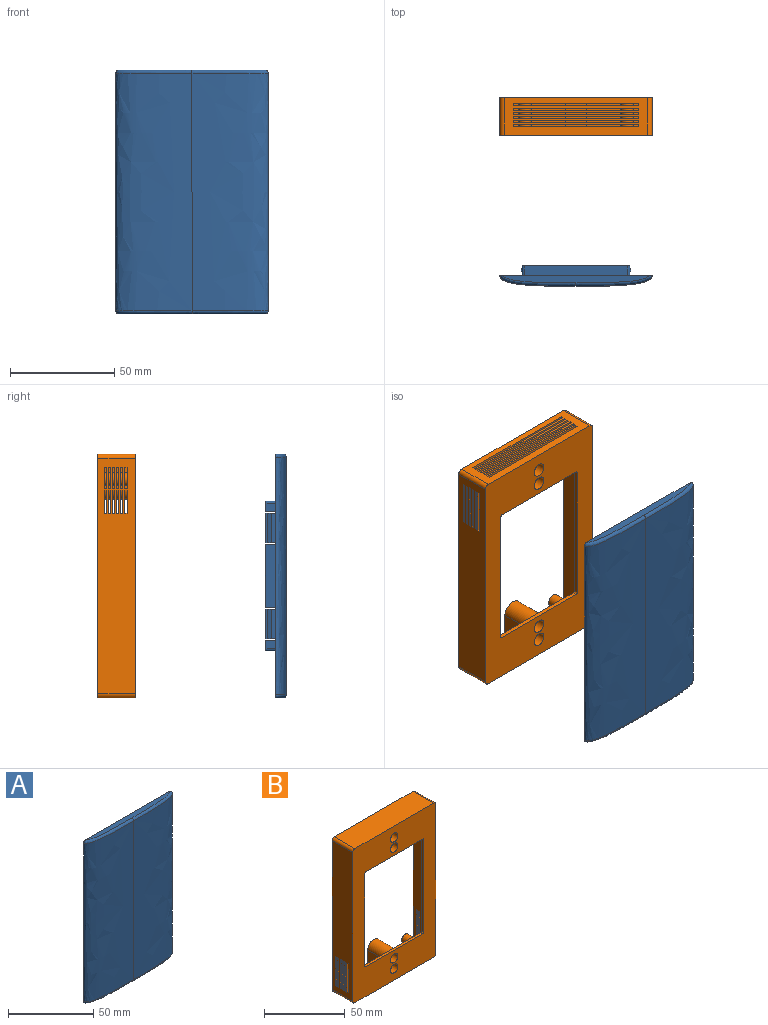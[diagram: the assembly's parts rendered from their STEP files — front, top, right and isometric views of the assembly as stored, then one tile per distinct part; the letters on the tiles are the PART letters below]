
ASSEMBLY  parts=2 mates=1
PART A: 93 faces, bbox 73.2x10.1x117.1 mm
  f0: plane 14x2.1mm, normal (1,0,0), area 29.4mm2, adj f37,f76,f78,f87
  f1: plane 14x0.7mm, normal (1,0,0), area 9.8mm2, adj f30,f74,f80,f86
  f2: plane 14x0.7mm, normal (-1,0,0), area 9.8mm2, adj f33,f67,f70,f84
  f3: plane 14x2.1mm, normal (-1,0,0), area 29.4mm2, adj f37,f65,f72,f81
  f4: plane 5x2.9mm, normal (1,0,0), area 14.5mm2, adj f37,f55,f56,f71
  f5: plane 30x5mm, normal (1,0,0), area 150mm2, adj f25,f37,f66,f69
  f6: plane 14x5mm, normal (1,0,0), area 70mm2, adj f22,f37,f67,f70
  f7: plane 14x5mm, normal (1,0,0), area 70mm2, adj f20,f37,f65,f72
  f8: plane 5x2.9mm, normal (-1,0,0), area 14.5mm2, adj f37,f45,f56,f79
  f9: plane 30x5mm, normal (-1,0,0), area 150mm2, adj f26,f37,f73,f77
  f10: plane 14x5mm, normal (-1,0,0), area 70mm2, adj f23,f37,f76,f78
  f11: plane 14x5mm, normal (-1,0,0), area 70mm2, adj f21,f37,f74,f80
  f12: plane 4.7x3.9mm, normal (-1,0,0), area 18.3mm2, adj f31,f37,f51,f71
  f13: plane 30x4.7mm, normal (-1,0,0), area 141mm2, adj f32,f37,f66,f69
  f14: plane 14x2.1mm, normal (-1,0,0), area 29.4mm2, adj f37,f67,f70,f83
  f15: plane 14x0.7mm, normal (-1,0,0), area 9.8mm2, adj f34,f65,f72,f82
  f16: plane 4.7x3.9mm, normal (1,0,0), area 18.3mm2, adj f27,f37,f53,f79
  f17: plane 30x4.7mm, normal (1,0,0), area 141mm2, adj f28,f37,f73,f77
  f18: plane 14x0.7mm, normal (1,0,0), area 9.8mm2, adj f29,f76,f78,f88
  f19: plane 14x2.1mm, normal (1,0,0), area 29.4mm2, adj f37,f74,f80,f85
  f20: plane 14x0.7mm, normal (0,1,0), area 9.8mm2, adj f7,f34,f65,f72
  f21: plane 14x0.7mm, normal (0,1,0), area 9.8mm2, adj f11,f30,f74,f80
  f22: plane 14x0.7mm, normal (0,1,0), area 9.8mm2, adj f6,f33,f67,f70
  f23: plane 14x0.7mm, normal (0,1,0), area 9.8mm2, adj f10,f29,f76,f78
  f24: plane 51.2x4.6mm, normal (0,1,0), area 41.5mm2, adj f40,f41,f42,f43,f44,f57,f58,f60
  f25: plane 30x0.7mm, normal (0,1,0), area 21mm2, adj f5,f32,f66,f69
  f26: plane 30x0.7mm, normal (0,1,0), area 21mm2, adj f9,f28,f73,f77
  f27: plane 3.9x0.3mm, normal (0.71,0.71,0), area 1.7mm2, adj f16,f56,f59,f79
  f28: plane 30x0.3mm, normal (0.71,0.71,0), area 12.7mm2, adj f17,f26,f73,f77
  f29: plane 14x0.3mm, normal (0.71,0.71,0), area 5.9mm2, adj f18,f23,f76,f78
  f30: plane 14x0.3mm, normal (0.71,0.71,0), area 5.9mm2, adj f1,f21,f74,f80
  f31: plane 3.9x0.3mm, normal (-0.71,0.71,0), area 1.7mm2, adj f12,f56,f63,f71
  f32: plane 30x0.3mm, normal (-0.71,0.71,0), area 12.7mm2, adj f13,f25,f66,f69
  f33: plane 14x0.3mm, normal (-0.71,0.71,0), area 5.9mm2, adj f2,f22,f67,f70
  f34: plane 14x0.3mm, normal (-0.71,0.71,0), area 5.9mm2, adj f15,f20,f65,f72
  f35: plane 70.1x3.55mm, normal (0,0,-1), area 209.6mm2, adj f37,f91,f92
  f36: plane 70.11x3.55mm, normal (0,0,1), area 209.6mm2, adj f37,f89,f90
  f37: plane 117.14x73.14mm, normal (0,1,0), area 8304mm2, adj f0,f3,f4,f5,f6,f7,f8,f9
  f38: bspline ~117x36.5mm, area 4331.7mm2, adj f37,f39,f89,f91
  f39: bspline ~117x36.5mm, area 4331.7mm2, adj f37,f38,f90,f92
  f40: plane 5x2.9mm, normal (1,0,0), area 14.5mm2, adj f24,f37,f41,f68
  f41: cylinder r=1mm len=5mm, axis (0,-1,0), area 7.9mm2, adj f24,f37,f40,f42
  f42: plane 47.8x5mm, normal (0,0,-1), area 239mm2, adj f24,f37,f41,f43
  f43: cylinder r=1mm len=5mm, axis (0,-1,0), area 7.9mm2, adj f24,f37,f42,f44
  f44: plane 5x2.9mm, normal (-1,0,0), area 14.5mm2, adj f24,f37,f43,f75
  f45: cylinder r=1mm len=5mm, axis (0,-1,0), area 7.9mm2, adj f8,f37,f46,f56
  f46: plane 47.8x5mm, normal (0,0,1), area 239mm2, adj f37,f45,f55,f56
  f47: cylinder r=1mm len=4.7mm, axis (0,-1,0), area 7.4mm2, adj f37,f48,f54,f58
  f48: plane 49.8x4.7mm, normal (0,0,1), area 234.1mm2, adj f37,f47,f49,f60
  f49: cylinder r=1mm len=4.7mm, axis (0,-1,0), area 7.4mm2, adj f37,f48,f50,f62
  f50: plane 4.7x3.9mm, normal (-1,0,0), area 18.3mm2, adj f37,f49,f64,f68
  f51: cylinder r=1mm len=4.7mm, axis (0,-1,0), area 7.4mm2, adj f12,f37,f52,f63
  f52: plane 49.8x4.7mm, normal (0,0,-1), area 234.1mm2, adj f37,f51,f53,f61
  f53: cylinder r=1mm len=4.7mm, axis (0,-1,0), area 7.4mm2, adj f16,f37,f52,f59
  f54: plane 4.7x3.9mm, normal (1,0,0), area 18.3mm2, adj f37,f47,f57,f75
  f55: cylinder r=1mm len=5mm, axis (0,-1,0), area 7.9mm2, adj f4,f37,f46,f56
  f56: plane 51.2x4.6mm, normal (0,1,0), area 41.5mm2, adj f4,f8,f27,f31,f45,f46,f55,f59
  f57: plane 3.9x0.3mm, normal (0.71,0.71,0), area 1.7mm2, adj f24,f54,f58,f75
  f58: cone r=1mm half-angle=45deg, axis (0,-1,0), area 0.6mm2, adj f24,f47,f57,f60
  f59: cone r=0.7mm half-angle=45deg, axis (0,-1,0), area 0.6mm2, adj f27,f53,f56,f61
  f60: plane 49.8x0.3mm, normal (0,0.71,0.71), area 21.1mm2, adj f24,f48,f58,f62
  f61: plane 49.8x0.3mm, normal (0,0.71,-0.71), area 21.1mm2, adj f52,f56,f59,f63
  f62: cone r=0.7mm half-angle=45deg, axis (0,-1,0), area 0.6mm2, adj f24,f49,f60,f64
  f63: cone r=1mm half-angle=45deg, axis (0,-1,0), area 0.6mm2, adj f31,f51,f56,f61
  f64: plane 3.9x0.3mm, normal (-0.71,0.71,0), area 1.7mm2, adj f24,f50,f62,f68
  f65: plane 5x1.48mm, normal (0,0,1), area 5.4mm2, adj f3,f7,f15,f20,f34,f37,f81,f82
  f66: plane 5x1mm, normal (0,0,-1), area 5mm2, adj f5,f13,f25,f32,f37
  f67: plane 5x1.48mm, normal (0,0,1), area 5.4mm2, adj f2,f6,f14,f22,f33,f37,f83,f84
  f68: plane 5x1mm, normal (0,0,-1), area 5mm2, adj f24,f37,f40,f50,f64
  f69: plane 5x1mm, normal (0,0,1), area 5mm2, adj f5,f13,f25,f32,f37
  f70: plane 5x1.48mm, normal (0,0,-1), area 5.4mm2, adj f2,f6,f14,f22,f33,f37,f83,f84
  f71: plane 5x1mm, normal (0,0,1), area 5mm2, adj f4,f12,f31,f37,f56
  f72: plane 5x1.48mm, normal (0,0,-1), area 5.4mm2, adj f3,f7,f15,f20,f34,f37,f81,f82
  f73: plane 5x1mm, normal (0,0,-1), area 5mm2, adj f9,f17,f26,f28,f37
  f74: plane 5x1.48mm, normal (0,0,1), area 5.4mm2, adj f1,f11,f19,f21,f30,f37,f85,f86
  f75: plane 5x1mm, normal (0,0,-1), area 5mm2, adj f24,f37,f44,f54,f57
  f76: plane 5x1.48mm, normal (0,0,1), area 5.4mm2, adj f0,f10,f18,f23,f29,f37,f87,f88
  f77: plane 5x1mm, normal (0,0,1), area 5mm2, adj f9,f17,f26,f28,f37
  f78: plane 5x1.48mm, normal (0,0,-1), area 5.4mm2, adj f0,f10,f18,f23,f29,f37,f87,f88
  f79: plane 5x1mm, normal (0,0,1), area 5mm2, adj f8,f16,f27,f37,f56
  f80: plane 5x1.48mm, normal (0,0,-1), area 5.4mm2, adj f1,f11,f19,f21,f30,f37,f85,f86
  f81: plane 14x0.48mm, normal (0,-1,0), area 6.6mm2, adj f3,f65,f72,f82
  f82: plane 14x1.9mm, normal (-0.97,0.24,0), area 27.4mm2, adj f15,f65,f72,f81
  f83: plane 14x0.48mm, normal (0,-1,0), area 6.6mm2, adj f14,f67,f70,f84
  f84: plane 14x1.9mm, normal (-0.97,0.24,0), area 27.4mm2, adj f2,f67,f70,f83
  f85: plane 14x0.48mm, normal (0,-1,0), area 6.6mm2, adj f19,f74,f80,f86
  f86: plane 14x1.9mm, normal (0.97,0.24,0), area 27.4mm2, adj f1,f74,f80,f85
  f87: plane 14x0.48mm, normal (0,-1,0), area 6.6mm2, adj f0,f76,f78,f88
  f88: plane 14x1.9mm, normal (0.97,0.24,0), area 27.4mm2, adj f18,f76,f78,f87
  f89: bspline ~50.22x5.07mm, area 84.3mm2, adj f36,f37,f38,f90
  f90: bspline ~39.95x5.07mm, area 84.3mm2, adj f36,f37,f39,f89
  f91: bspline ~50.22x5.07mm, area 84.3mm2, adj f35,f37,f38,f92
  f92: bspline ~39.95x5.07mm, area 84.3mm2, adj f35,f37,f39,f91
PART B: 141 faces, bbox 73x18x117 mm
  f0: plane 113x18mm, normal (-1,0,0), area 1902mm2, adj f8,f9,f91,f92,f93,f94,f95,f96
  f1: plane 109x16mm, normal (1,0,0), area 1612mm2, adj f8,f68,f86,f87,f93,f94,f95,f96
  f2: plane 10.5x1mm, normal (0,0,-1), area 10.5mm2, adj f13,f15,f64,f66
  f3: plane 10.5x1mm, normal (0,0,-1), area 10.5mm2, adj f17,f19,f64,f66
  f4: plane 10.5x1mm, normal (0,0,-1), area 10.5mm2, adj f21,f23,f64,f66
  f5: plane 10.5x1mm, normal (0,0,-1), area 10.5mm2, adj f25,f27,f64,f66
  f6: plane 10.5x1mm, normal (0,0,-1), area 10.5mm2, adj f29,f31,f64,f66
  f7: plane 10.5x1mm, normal (0,0,-1), area 10.5mm2, adj f34,f36,f64,f66
  f8: plane 117x73mm, normal (0,1,0), area 1084.8mm2, adj f0,f1,f10,f11,f12,f53,f54,f55
  f9: plane 117x73mm, normal (0,-1,0), area 4661.7mm2, adj f0,f10,f11,f12,f37,f38,f39,f40
  f10: plane 69x18mm, normal (0,0,-1), area 882mm2, adj f8,f9,f13,f14,f15,f16,f17,f18
  f11: plane 113x18mm, normal (1,0,0), area 1902mm2, adj f8,f9,f89,f90,f117,f118,f119,f120
  f12: plane 69x18mm, normal (0,0,1), area 1242mm2, adj f8,f9,f90,f91
  f13: plane 60x2mm, normal (0,1,0), area 120mm2, adj f2,f10,f14,f16,f63,f67
  f14: plane 2x1mm, normal (1,0,0), area 2mm2, adj f10,f13,f15,f63
  f15: plane 60x2mm, normal (0,-1,0), area 120mm2, adj f2,f10,f14,f16,f63,f67
  f16: plane 2x1mm, normal (-1,0,0), area 2mm2, adj f10,f13,f15,f67
  f17: plane 60x2mm, normal (0,1,0), area 120mm2, adj f3,f10,f18,f20,f63,f67
  f18: plane 2x1mm, normal (1,0,0), area 2mm2, adj f10,f17,f19,f63
  f19: plane 60x2mm, normal (0,-1,0), area 120mm2, adj f3,f10,f18,f20,f63,f67
  f20: plane 2x1mm, normal (-1,0,0), area 2mm2, adj f10,f17,f19,f67
  f21: plane 60x2mm, normal (0,1,0), area 120mm2, adj f4,f10,f22,f24,f63,f67
  f22: plane 2x1mm, normal (1,0,0), area 2mm2, adj f10,f21,f23,f63
  f23: plane 60x2mm, normal (0,-1,0), area 120mm2, adj f4,f10,f22,f24,f63,f67
  f24: plane 2x1mm, normal (-1,0,0), area 2mm2, adj f10,f21,f23,f67
  f25: plane 60x2mm, normal (0,1,0), area 120mm2, adj f5,f10,f26,f28,f63,f67
  f26: plane 2x1mm, normal (1,0,0), area 2mm2, adj f10,f25,f27,f63
  f27: plane 60x2mm, normal (0,-1,0), area 120mm2, adj f5,f10,f26,f28,f63,f67
  f28: plane 2x1mm, normal (-1,0,0), area 2mm2, adj f10,f25,f27,f67
  f29: plane 60x2mm, normal (0,1,0), area 120mm2, adj f6,f10,f30,f32,f63,f67
  f30: plane 2x1mm, normal (1,0,0), area 2mm2, adj f10,f29,f31,f63
  f31: plane 60x2mm, normal (0,-1,0), area 120mm2, adj f6,f10,f30,f32,f63,f67
  f32: plane 2x1mm, normal (-1,0,0), area 2mm2, adj f10,f29,f31,f67
  f33: plane 2x1mm, normal (-1,0,0), area 2mm2, adj f10,f34,f36,f67
  f34: plane 60x2mm, normal (0,1,0), area 120mm2, adj f7,f10,f33,f35,f63,f67
  f35: plane 2x1mm, normal (1,0,0), area 2mm2, adj f10,f34,f36,f63
  f36: plane 60x2mm, normal (0,-1,0), area 120mm2, adj f7,f10,f33,f35,f63,f67
  f37: plane 70x2mm, normal (-1,0,0), area 140mm2, adj f9,f38,f44,f68
  f38: cylinder r=1mm len=2mm, axis (0,-1,0), area 3.1mm2, adj f9,f37,f39,f68
  f39: plane 50x2mm, normal (0,0,-1), area 100mm2, adj f9,f38,f40,f68
  f40: cylinder r=1mm len=2mm, axis (0,-1,0), area 3.1mm2, adj f9,f39,f41,f68
  f41: plane 70x2mm, normal (1,0,0), area 140mm2, adj f9,f40,f42,f68
  f42: cylinder r=1mm len=2mm, axis (0,-1,0), area 3.1mm2, adj f9,f41,f43,f68
  f43: plane 50x2mm, normal (0,0,1), area 100mm2, adj f9,f42,f44,f68
  f44: cylinder r=1mm len=2mm, axis (0,-1,0), area 3.1mm2, adj f9,f37,f43,f68
  f45: cylinder r=3.25mm len=15mm, axis (0,-1,0), area 306.3mm2, adj f9,f46
  f46: plane 6.5x6.5mm, normal (0,-1,0), area 20.6mm2, adj f45,f56
  f47: cylinder r=3.25mm len=15mm, axis (0,-1,0), area 306.3mm2, adj f9,f48
  f48: plane 6.5x6.5mm, normal (0,-1,0), area 20.6mm2, adj f47,f55
  f49: cylinder r=3.25mm len=15mm, axis (0,-1,0), area 306.3mm2, adj f9,f50
  f50: plane 6.5x6.5mm, normal (0,-1,0), area 20.6mm2, adj f49,f54
  f51: cylinder r=3.25mm len=15mm, axis (0,-1,0), area 306.3mm2, adj f9,f52
  f52: plane 6.5x6.5mm, normal (0,-1,0), area 20.6mm2, adj f51,f53
  f53: cylinder r=2mm len=4mm, axis (0,1,0), area 37.7mm2, adj f8,f52
  f54: cylinder r=2mm len=4mm, axis (0,1,0), area 37.7mm2, adj f8,f50
  f55: cylinder r=2mm len=4mm, axis (0,1,0), area 37.7mm2, adj f8,f48
  f56: cylinder r=2mm len=4mm, axis (0,1,0), area 37.7mm2, adj f8,f46
  f57: plane 109x16mm, normal (-1,0,0), area 1612mm2, adj f8,f68,f85,f88,f117,f118,f119,f120
  f58: plane 27.25x16mm, normal (0,0,-1), area 436mm2, adj f8,f59,f68,f85
  f59: plane 16x14.5mm, normal (1,0,0), area 232mm2, adj f8,f58,f60,f68
  f60: cylinder r=5.25mm len=16mm, axis (0,1,0), area 263.9mm2, adj f8,f59,f61,f68
  f61: plane 16x14.5mm, normal (-1,0,0), area 232mm2, adj f8,f60,f62,f68
  f62: plane 27.25x16mm, normal (0,0,-1), area 436mm2, adj f8,f61,f68,f86
  f63: plane 27.25x16mm, normal (0,0,1), area 287.5mm2, adj f8,f13,f14,f15,f17,f18,f19,f21
  f64: plane 16x14.5mm, normal (-1,0,0), area 232mm2, adj f2,f3,f4,f5,f6,f7,f8,f63
  f65: cylinder r=5.25mm len=16mm, axis (0,1,0), area 263.9mm2, adj f8,f64,f66,f68
  f66: plane 16x14.5mm, normal (1,0,0), area 232mm2, adj f2,f3,f4,f5,f6,f7,f8,f65
  f67: plane 27.25x16mm, normal (0,0,1), area 287.5mm2, adj f8,f13,f15,f16,f17,f19,f20,f21
  f68: plane 113x69mm, normal (0,1,0), area 3546.2mm2, adj f1,f37,f38,f39,f40,f41,f42,f43
  f69: cylinder r=1.15mm len=13mm, axis (0,-1,0), area 93.9mm2, adj f71,f72
  f70: cylinder r=3mm len=13mm, axis (0,-1,0), area 245mm2, adj f68,f71
  f71: plane 6x6mm, normal (0,1,0), area 24.1mm2, adj f69,f70
  f72: plane 2.3x2.3mm, normal (0,1,0), area 4.2mm2, adj f69
  f73: cylinder r=3mm len=13mm, axis (0,-1,0), area 245mm2, adj f68,f75
  f74: cylinder r=1.15mm len=13mm, axis (0,-1,0), area 93.9mm2, adj f75,f76
  f75: plane 6x6mm, normal (0,1,0), area 24.1mm2, adj f73,f74
  f76: plane 2.3x2.3mm, normal (0,1,0), area 4.2mm2, adj f74
  f77: cylinder r=3mm len=13mm, axis (0,-1,0), area 245mm2, adj f68,f79
  f78: cylinder r=1.15mm len=13mm, axis (0,-1,0), area 93.9mm2, adj f79,f80
  f79: plane 6x6mm, normal (0,1,0), area 24.1mm2, adj f77,f78
  f80: plane 2.3x2.3mm, normal (0,1,0), area 4.2mm2, adj f78
  f81: cylinder r=1.15mm len=13mm, axis (0,-1,0), area 93.9mm2, adj f83,f84
  f82: cylinder r=3mm len=13mm, axis (0,-1,0), area 245mm2, adj f68,f83
  f83: plane 6x6mm, normal (0,1,0), area 24.1mm2, adj f81,f82
  f84: plane 2.3x2.3mm, normal (0,1,0), area 4.2mm2, adj f81
  f85: cylinder r=2mm len=16mm, axis (0,1,0), area 50.3mm2, adj f8,f57,f58,f68
  f86: cylinder r=2mm len=16mm, axis (0,-1,0), area 50.3mm2, adj f1,f8,f62,f68
  f87: cylinder r=2mm len=16mm, axis (0,1,0), area 50.3mm2, adj f1,f8,f63,f68
  f88: cylinder r=2mm len=16mm, axis (0,-1,0), area 50.3mm2, adj f8,f57,f67,f68
  f89: cylinder r=2mm len=18mm, axis (0,-1,0), area 56.5mm2, adj f8,f9,f10,f11
  f90: cylinder r=2mm len=18mm, axis (0,1,0), area 56.5mm2, adj f8,f9,f11,f12
  f91: cylinder r=2mm len=18mm, axis (0,-1,0), area 56.5mm2, adj f0,f8,f9,f12
  f92: cylinder r=2mm len=18mm, axis (0,1,0), area 56.5mm2, adj f0,f8,f9,f10
  f93: plane 22x2mm, normal (0,1,0), area 44mm2, adj f0,f1,f94,f96
  f94: plane 2x1mm, normal (0,0,-1), area 2mm2, adj f0,f1,f93,f95
  f95: plane 22x2mm, normal (0,-1,0), area 44mm2, adj f0,f1,f94,f96
  f96: plane 2x1mm, normal (0,0,1), area 2mm2, adj f0,f1,f93,f95
  f97: plane 22x2mm, normal (0,1,0), area 44mm2, adj f0,f1,f98,f100
  f98: plane 2x1mm, normal (0,0,-1), area 2mm2, adj f0,f1,f97,f99
  f99: plane 22x2mm, normal (0,-1,0), area 44mm2, adj f0,f1,f98,f100
  f100: plane 2x1mm, normal (0,0,1), area 2mm2, adj f0,f1,f97,f99
  f101: plane 22x2mm, normal (0,1,0), area 44mm2, adj f0,f1,f102,f104
  f102: plane 2x1mm, normal (0,0,-1), area 2mm2, adj f0,f1,f101,f103
  f103: plane 22x2mm, normal (0,-1,0), area 44mm2, adj f0,f1,f102,f104
  f104: plane 2x1mm, normal (0,0,1), area 2mm2, adj f0,f1,f101,f103
  f105: plane 22x2mm, normal (0,1,0), area 44mm2, adj f0,f1,f106,f108
  f106: plane 2x1mm, normal (0,0,-1), area 2mm2, adj f0,f1,f105,f107
  f107: plane 22x2mm, normal (0,-1,0), area 44mm2, adj f0,f1,f106,f108
  f108: plane 2x1mm, normal (0,0,1), area 2mm2, adj f0,f1,f105,f107
  f109: plane 22x2mm, normal (0,1,0), area 44mm2, adj f0,f1,f110,f112
  f110: plane 2x1mm, normal (0,0,-1), area 2mm2, adj f0,f1,f109,f111
  f111: plane 22x2mm, normal (0,-1,0), area 44mm2, adj f0,f1,f110,f112
  f112: plane 2x1mm, normal (0,0,1), area 2mm2, adj f0,f1,f109,f111
  f113: plane 22x2mm, normal (0,1,0), area 44mm2, adj f0,f1,f114,f116
  f114: plane 2x1mm, normal (0,0,-1), area 2mm2, adj f0,f1,f113,f115
  f115: plane 22x2mm, normal (0,-1,0), area 44mm2, adj f0,f1,f114,f116
  f116: plane 2x1mm, normal (0,0,1), area 2mm2, adj f0,f1,f113,f115
  f117: plane 22x2mm, normal (0,1,0), area 44mm2, adj f11,f57,f118,f120
  f118: plane 2x1mm, normal (0,0,1), area 2mm2, adj f11,f57,f117,f119
  f119: plane 22x2mm, normal (0,-1,0), area 44mm2, adj f11,f57,f118,f120
  f120: plane 2x1mm, normal (0,0,-1), area 2mm2, adj f11,f57,f117,f119
  f121: plane 22x2mm, normal (0,1,0), area 44mm2, adj f11,f57,f122,f124
  f122: plane 2x1mm, normal (0,0,1), area 2mm2, adj f11,f57,f121,f123
  f123: plane 22x2mm, normal (0,-1,0), area 44mm2, adj f11,f57,f122,f124
  f124: plane 2x1mm, normal (0,0,-1), area 2mm2, adj f11,f57,f121,f123
  f125: plane 22x2mm, normal (0,1,0), area 44mm2, adj f11,f57,f126,f128
  f126: plane 2x1mm, normal (0,0,1), area 2mm2, adj f11,f57,f125,f127
  f127: plane 22x2mm, normal (0,-1,0), area 44mm2, adj f11,f57,f126,f128
  f128: plane 2x1mm, normal (0,0,-1), area 2mm2, adj f11,f57,f125,f127
  f129: plane 22x2mm, normal (0,1,0), area 44mm2, adj f11,f57,f130,f132
  f130: plane 2x1mm, normal (0,0,1), area 2mm2, adj f11,f57,f129,f131
  f131: plane 22x2mm, normal (0,-1,0), area 44mm2, adj f11,f57,f130,f132
  f132: plane 2x1mm, normal (0,0,-1), area 2mm2, adj f11,f57,f129,f131
  f133: plane 22x2mm, normal (0,1,0), area 44mm2, adj f11,f57,f134,f136
  f134: plane 2x1mm, normal (0,0,1), area 2mm2, adj f11,f57,f133,f135
  f135: plane 22x2mm, normal (0,-1,0), area 44mm2, adj f11,f57,f134,f136
  f136: plane 2x1mm, normal (0,0,-1), area 2mm2, adj f11,f57,f133,f135
  f137: plane 22x2mm, normal (0,1,0), area 44mm2, adj f11,f57,f138,f140
  f138: plane 2x1mm, normal (0,0,1), area 2mm2, adj f11,f57,f137,f139
  f139: plane 22x2mm, normal (0,-1,0), area 44mm2, adj f11,f57,f138,f140
  f140: plane 2x1mm, normal (0,0,-1), area 2mm2, adj f11,f57,f137,f139
PLACE A t=(-54.97,-7,135.1)mm
PLACE B rot(axis=(0,1,0),180deg) t=(-54.97,48.31,135.1)mm
MATE slider B.f9 <-> A.f37  axis (0,-1,0) through (-54.97,30.31,135.1)mm
